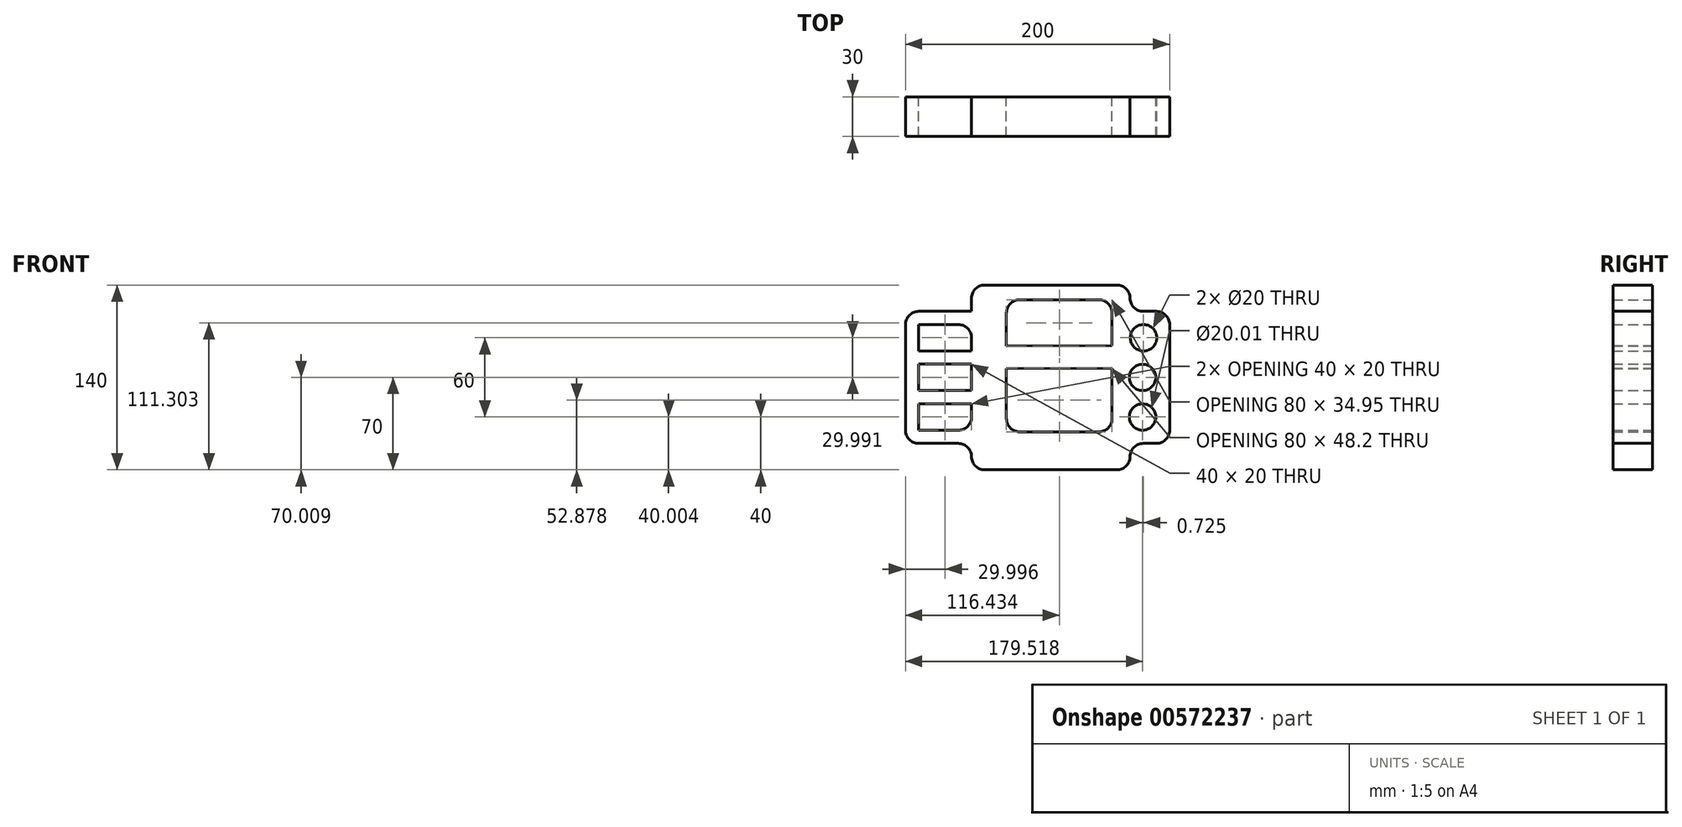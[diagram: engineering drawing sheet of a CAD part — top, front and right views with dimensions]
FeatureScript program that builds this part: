
annotation { "Feature Type Name" : "Feature", "Feature Type Description" : "" }
export const myFeature = defineFeature(function(context is Context, id is Id, definition is map)
    precondition{}
    {
        {
            var Q0;
            Q0=qCreatedBy(makeId("Front.planeOp"),FACE);
            var sketch = newSketch(context, id + "F0", { "sketchPlane" : qUnion([Q0])});
            skLineSegment(sketch, "E0", {"start": v(-43.91, 60) * mm, "end": v(56.09, 60) * mm});
            skLineSegment(sketch, "E1", {"start": v(66.09, 50) * mm, "end": v(66.09, 50) * mm});
            skLineSegment(sketch, "E2", {"start": v(76.09, 40) * mm, "end": v(86.09, 40) * mm});
            skLineSegment(sketch, "E3", {"start": v(96.09, 30) * mm, "end": v(96.09, -50) * mm});
            skLineSegment(sketch, "E4", {"start": v(86.09, -60) * mm, "end": v(76.09, -60) * mm});
            skLineSegment(sketch, "E5", {"start": v(66.09, -70) * mm, "end": v(66.09, -70) * mm});
            skLineSegment(sketch, "E6", {"start": v(56.09, -80) * mm, "end": v(-43.91, -80) * mm});
            skLineSegment(sketch, "E7", {"start": v(-53.91, -70) * mm, "end": v(-53.91, -70) * mm});
            skLineSegment(sketch, "E8", {"start": v(-63.91, -60) * mm, "end": v(-93.91, -60) * mm});
            skLineSegment(sketch, "E9", {"start": v(-103.91, -50) * mm, "end": v(-103.91, 30) * mm});
            skLineSegment(sketch, "E10", {"start": v(-93.91, 40) * mm, "end": v(-53.91, 40) * mm});
            skLineSegment(sketch, "E11", {"start": v(-53.91, 40) * mm, "end": v(-53.91, 50) * mm});
            skCircle(sketch, "E12", {"center": v(76.33, 20) * mm, "radius": 10 * mm});
            skCircle(sketch, "E13", {"center": v(75.6, -40) * mm, "radius": 10 * mm});
            skPoint(sketch, "E14.orphan", {"position": v(-51.14, -20) * mm});
            skPoint(sketch, "E15.orphan", {"position": v(-51.14, -10) * mm});
            skPoint(sketch, "E16.end.orphan", {"position": v(-51.14, 0) * mm});
            skPoint(sketch, "E17.end.orphan", {"position": v(-83.53, 20) * mm});
            skPoint(sketch, "E17.start.orphan", {"position": v(-83.53, 0) * mm});
            skPoint(sketch, "E18.orphan", {"position": v(-83.53, -10) * mm});
            skPoint(sketch, "E19.end.orphan", {"position": v(-83.53, -40) * mm});
            skPoint(sketch, "E20.end.orphan", {"position": v(-83.53, -20) * mm});
            skPoint(sketch, "E20.start.orphan", {"position": v(-83.53, -30) * mm});
            skLineSegment(sketch, "E21", {"start": v(-93.91, 30) * mm, "end": v(-63.91, 30) * mm});
            skLineSegment(sketch, "E22", {"start": v(-53.91, 20) * mm, "end": v(-53.91, 10) * mm});
            skLineSegment(sketch, "E23", {"start": v(-53.91, 10) * mm, "end": v(-93.91, 10) * mm});
            skLineSegment(sketch, "E24", {"start": v(-93.91, 10) * mm, "end": v(-93.91, 30) * mm});
            skLineSegment(sketch, "E25", {"start": v(-93.91, 0) * mm, "end": v(-53.91, 0) * mm});
            skLineSegment(sketch, "E26", {"start": v(-53.91, 0) * mm, "end": v(-53.91, -20) * mm});
            skLineSegment(sketch, "E27", {"start": v(-53.91, -20) * mm, "end": v(-93.91, -20) * mm});
            skLineSegment(sketch, "E28", {"start": v(-93.91, -20) * mm, "end": v(-93.91, 0) * mm});
            skLineSegment(sketch, "E29", {"start": v(-93.91, -30) * mm, "end": v(-53.91, -30) * mm});
            skLineSegment(sketch, "E30", {"start": v(-53.91, -30) * mm, "end": v(-53.91, -40) * mm});
            skLineSegment(sketch, "E31", {"start": v(-63.91, -50) * mm, "end": v(-93.91, -50) * mm});
            skLineSegment(sketch, "E32", {"start": v(-93.91, -50) * mm, "end": v(-93.91, -30) * mm});
            skPoint(sketch, "E33.end.orphan", {"position": v(-27.48, 48.78) * mm});
            skPoint(sketch, "E34.end.orphan", {"position": v(-32.87, 26.84) * mm});
            skPoint(sketch, "E35.end.orphan", {"position": v(-32.87, -45.4) * mm});
            skPoint(sketch, "E36.end.orphan", {"position": v(-27.48, -51.22) * mm});
            skPoint(sketch, "E37.end.orphan", {"position": v(52.52, -51.22) * mm});
            skPoint(sketch, "E38.end.orphan", {"position": v(54.74, -45.4) * mm});
            skPoint(sketch, "E39.end.orphan", {"position": v(54.74, 26.84) * mm});
            skPoint(sketch, "E39.start.orphan", {"position": v(52.52, 48.78) * mm});
            skLineSegment(sketch, "E40", {"start": v(-17.48, 48.78) * mm, "end": v(42.52, 48.78) * mm});
            skLineSegment(sketch, "E41", {"start": v(42.52, -51.22) * mm, "end": v(-17.48, -51.22) * mm});
            skLineSegment(sketch, "E42", {"start": v(52.52, -41.22) * mm, "end": v(52.52, -3.02) * mm});
            skLineSegment(sketch, "E43", {"start": v(-27.48, 38.78) * mm, "end": v(-27.48, 13.83) * mm});
            skCircle(sketch, "E44", {"center": v(75.6, -10) * mm, "radius": 10 * mm});
            skPoint(sketch, "E45.visualSharp", {"position": v(-53.91, 30) * mm});
            skArc(sketch, "E45.filletArc", {"start": v(-53.91, 20) * mm, "mid": v(-56.84, 27.07) * mm, "end": v(-63.91, 30) * mm});
            skPoint(sketch, "E46.visualSharp", {"position": v(-53.91, -50) * mm});
            skArc(sketch, "E46.filletArc", {"start": v(-63.91, -50) * mm, "mid": v(-56.84, -47.07) * mm, "end": v(-53.91, -40) * mm});
            skArc(sketch, "E47.filletArc", {"start": v(52.52, 38.78) * mm, "mid": v(49.6, 45.85) * mm, "end": v(42.52, 48.78) * mm});
            skArc(sketch, "E48.filletArc", {"start": v(-17.48, 48.78) * mm, "mid": v(-24.55, 45.85) * mm, "end": v(-27.48, 38.78) * mm});
            skArc(sketch, "E49.filletArc", {"start": v(-27.48, -41.22) * mm, "mid": v(-24.55, -48.3) * mm, "end": v(-17.48, -51.22) * mm});
            skArc(sketch, "E50.filletArc", {"start": v(42.52, -51.22) * mm, "mid": v(49.6, -48.3) * mm, "end": v(52.52, -41.22) * mm});
            skLineSegment(sketch, "E51", {"start": v(52.52, 14.24) * mm, "end": v(52.52, 38.78) * mm});
            skLineSegment(sketch, "E52", {"start": v(-27.48, -3.44) * mm, "end": v(-27.48, -41.22) * mm});
            skLineSegment(sketch, "E53", {"start": v(-27.48, 13.83) * mm, "end": v(52.52, 14.24) * mm});
            skLineSegment(sketch, "E54", {"start": v(-27.48, -3.44) * mm, "end": v(52.52, -3.02) * mm});
            skPoint(sketch, "E55.visualSharp", {"position": v(66.09, 60) * mm});
            skArc(sketch, "E55.filletArc", {"start": v(66.09, 50) * mm, "mid": v(63.16, 57.07) * mm, "end": v(56.09, 60) * mm});
            skPoint(sketch, "E56.visualSharp", {"position": v(66.09, 40) * mm});
            skArc(sketch, "E56.filletArc", {"start": v(66.09, 50) * mm, "mid": v(69.01, 42.93) * mm, "end": v(76.09, 40) * mm});
            skPoint(sketch, "E57.visualSharp", {"position": v(96.09, 40) * mm});
            skArc(sketch, "E57.filletArc", {"start": v(96.09, 30) * mm, "mid": v(93.16, 37.07) * mm, "end": v(86.09, 40) * mm});
            skPoint(sketch, "E58.visualSharp", {"position": v(96.09, -60) * mm});
            skArc(sketch, "E58.filletArc", {"start": v(86.09, -60) * mm, "mid": v(93.16, -57.07) * mm, "end": v(96.09, -50) * mm});
            skPoint(sketch, "E59.visualSharp", {"position": v(66.09, -60) * mm});
            skArc(sketch, "E59.filletArc", {"start": v(76.09, -60) * mm, "mid": v(69.01, -62.93) * mm, "end": v(66.09, -70) * mm});
            skPoint(sketch, "E60.visualSharp", {"position": v(66.09, -80) * mm});
            skArc(sketch, "E60.filletArc", {"start": v(56.09, -80) * mm, "mid": v(63.16, -77.07) * mm, "end": v(66.09, -70) * mm});
            skPoint(sketch, "E61.visualSharp", {"position": v(-53.91, -80) * mm});
            skArc(sketch, "E61.filletArc", {"start": v(-53.91, -70) * mm, "mid": v(-50.99, -77.07) * mm, "end": v(-43.91, -80) * mm});
            skPoint(sketch, "E62.visualSharp", {"position": v(-53.91, 60) * mm});
            skArc(sketch, "E62.filletArc", {"start": v(-43.91, 60) * mm, "mid": v(-50.99, 57.07) * mm, "end": v(-53.91, 50) * mm});
            skPoint(sketch, "E63.visualSharp", {"position": v(-103.91, 40) * mm});
            skArc(sketch, "E63.filletArc", {"start": v(-93.91, 40) * mm, "mid": v(-100.99, 37.07) * mm, "end": v(-103.91, 30) * mm});
            skPoint(sketch, "E64.visualSharp", {"position": v(-103.91, -60) * mm});
            skArc(sketch, "E64.filletArc", {"start": v(-103.91, -50) * mm, "mid": v(-100.99, -57.07) * mm, "end": v(-93.91, -60) * mm});
            skPoint(sketch, "E65.visualSharp", {"position": v(-53.91, -60) * mm});
            skArc(sketch, "E65.filletArc", {"start": v(-53.91, -70) * mm, "mid": v(-56.84, -62.93) * mm, "end": v(-63.91, -60) * mm});
            skSolve(sketch);
        }
        {
            var Q0;
            Q0 = qSketchRegion(id + "F0", true);
            extrude(context, id + "F1", {"entities" : qUnion([Q0]), "depth" : 30 * mm, "offsetDistance" : 25 * mm});
        }
    });
